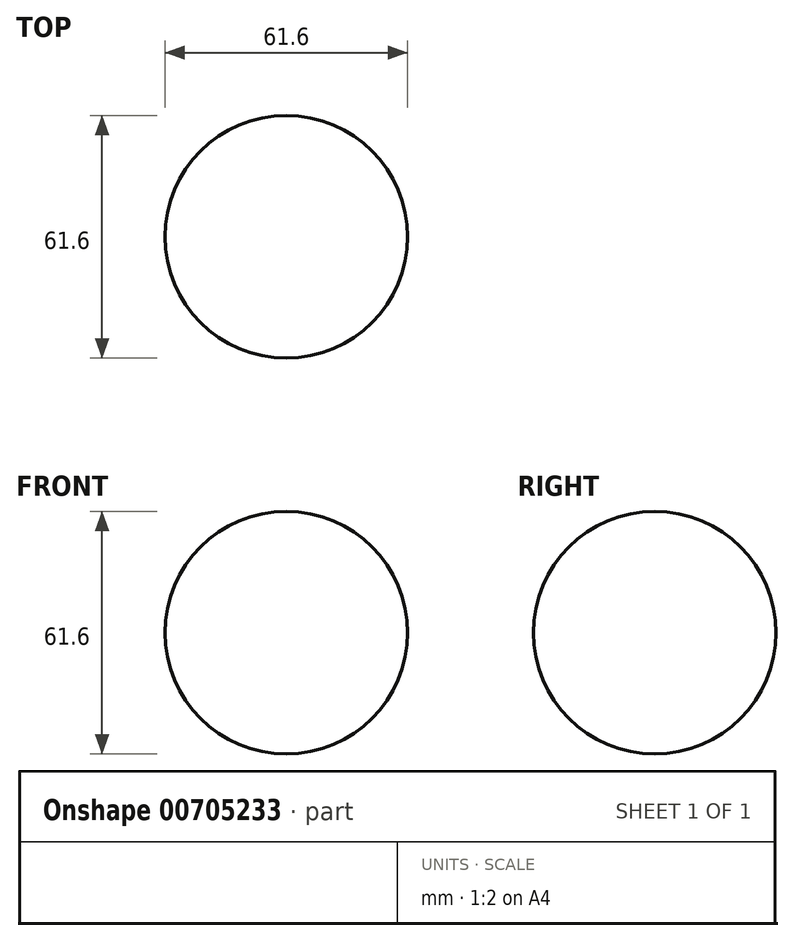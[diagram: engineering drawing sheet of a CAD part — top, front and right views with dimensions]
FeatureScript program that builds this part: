
annotation { "Feature Type Name" : "Feature", "Feature Type Description" : "" }
export const myFeature = defineFeature(function(context is Context, id is Id, definition is map)
    precondition{}
    {
        {
            var Q0;
            Q0=qCreatedBy(makeId("Front.planeOp"),FACE);
            var sketch = newSketch(context, id + "F0", { "sketchPlane" : qUnion([Q0])});
            skArc(sketch, "E0", {"start": v(0, 30.8) * mm, "mid": v(-30.8, 0) * mm, "end": v(0, -30.8) * mm});
            skLineSegment(sketch, "E1", {"start": v(0, 0) * mm, "end": v(0, 30.8) * mm});
            skLineSegment(sketch, "E2", {"start": v(0, 30.8) * mm, "end": v(0, -30.8) * mm});
            skSolve(sketch);
        }
        {
            var Q0;
            Q0 = qSketchRegion(id + "F0", true);
            var Q1;
            Q1=sQuery(id+"F0.wireOp",EDGE,"E2");
            revolve(context, id + "F1", {"surfaceOperationType" : NewSurfaceOperationType.NEW, "entities" : qUnion([Q0]), "axis" : qUnion([Q1]), "revolveType" : RevolveType.FULL});
        }
    });
